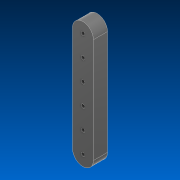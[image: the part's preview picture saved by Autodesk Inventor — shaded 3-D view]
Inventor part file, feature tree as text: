
AUTODESK INVENTOR PART (.ipt)
format: ipt  version: 2022.2 (Build 262287000, 287)  size: 96,768 bytes
history: native  units: in
note: dims shown in document units (in); Inventor stores cm internally (conversion verified against a paired STEP export)
features: sketch x1, extrude x1, hole x1
ambient origin geometry x8: Origin, YZ Plane, XZ Plane, XY Plane, X Axis, Y Axis, Z Axis, Center Point
bodies: Solid1 (feature_tree)
feature tree (3):
  sketch  "Sketch1"  dims[d0=2.5in d1=1.0in d2=1.0in d3=1.0in d4=1.0in d5=1.0in d6=0.675in d7=0.0in d8=0.17in d9=0.75in d10=0.375in d11=0.25in d12=0.5635in d13=1.0in d14=0.8108in]
  extrude  "Extrusion1"  Depth=1.0in
  hole  "Hole1"  [1 undecoded]
note: 1 required parameter value undecoded (feature->parameter linkage not recoverable at this tier; creation-order binding heuristic only, values carry confidence <= 0.55)
